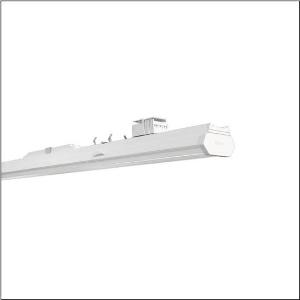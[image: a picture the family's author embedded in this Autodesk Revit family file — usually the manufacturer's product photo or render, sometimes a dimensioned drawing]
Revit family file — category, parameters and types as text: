
# Revit family: licross_r__11_protected_ho_51td12dn4fxm3c_9ee7
name_source: partatom
category: Lighting Fixtures
units: mm (PartAtom-declared; Revit-internal decimal feet)

## family parameters
Cut with Voids When Loaded = No
Host = Face
Light Source = No
Part Type = Normal
Room Calculation Point = No
Round Connector Dimension = Use Diameter
Shared = No

## types (1)
- --- (1 x LED, 970 lm, 7.4 W, 4000K)
    Apparent Load = 7 VA
    CIE Flux Codes = 70 91 97 98 100
    Color Rendering = 80
    Color Temperature = 4000K
    Default Elevation = 1800 mm
    Description = Licross® 11 Protected HO, luminaire insert, of sheet steel, galvanised, coil coated, white, length: 1.500mm, width: 90mm, height: 101mm, LED rated luminous flux: 15.270lm, light colour: 840, SDCM (Standard Deviation of Colour Matching)MacAdam ≤ 2 SDCM (initial), control gear: DALI 2 (for two DALI lines), with plug, 6-pole, with phase selection, for trunking rail, 14-core, mains connection: 220..240V, AC, 50/60Hz, rated input power: 91W, for trunking rail, 14-core, internal wiring halogen-free, for emergency light function, converter,control gear: single battery element, battery: LiFePO4, 9Ah, primary light control with lens, of plastic, primary optical cover: cover, of PMMA, light emission: direct distribution, primary light characteristic: symmetric, protection rating (complete): IP54, insulation class (complete): insulation class I (protective earthing), certification: CE, UKCA, protection symbol: D if used in an environment with non-conductive dust loads with corresponding accessories, impact resistance: IK06, permissible ambient temperature for indoor applications: +5..+30°C, standard: EN 60598-2-22, LABS conformity tested according to VDMA 24364:2018-05, reducing of maximum allowable ambient temperature of 5°C with ceiling mounting, corresponds to IFS (International Featured Standards) requirements for safety and quality in the food industry, packaging unit: 1 piece
    Height = 92 mm
    Lamp = 1 x LED
    Lamp Light Flux = 970 lm
    Lamp Power = 7.4 W
    Lamp count = 1
    Length = 1500 mm
    Luminous efficacy = 131 lm/W
    Manufacturer = Siteco
    ModVariant = No
    Model = 51TD12DN4FXM3C
    Mounting Place = Ceiling
    Mounting Type = Pendant
    Number of Poles = 1
    OnlyDefault = Yes
    Power Factor = 1
    Product Name = Licross® 11 Protected HO
    Product group = luminaire insert | ceiling pendant
    ProductGroupID = 901
    Protection Class = Protection class I
    Protection Degree = IP 54
    RLX_Detail_Level = 1
    RLX_Emergency_Light_Flux = 0 lm
    RLX_Emergency_Type = 0
    RLX_Emergency_Type_DB = No
    RlxData = <blob elided: 25053 chars, md5=b5ed9d7f>
    Socket = socket
    Standby Power = 0 W
    System Light Flux = 970 lm
    System Power = 7 W
    Type Comments = : emergency light operation: 3 h
    Type Image = l_1256145.jpg
    URL = http://relux.com
    VarID = @adj_098705
    Voltage = 0 V
    Weight = 0.00 kg
    Width = 88 mm

## geometry (parser evidence)
native form markers: Blend x4, Sweep x11
no freeform markers — native parametric forms only
